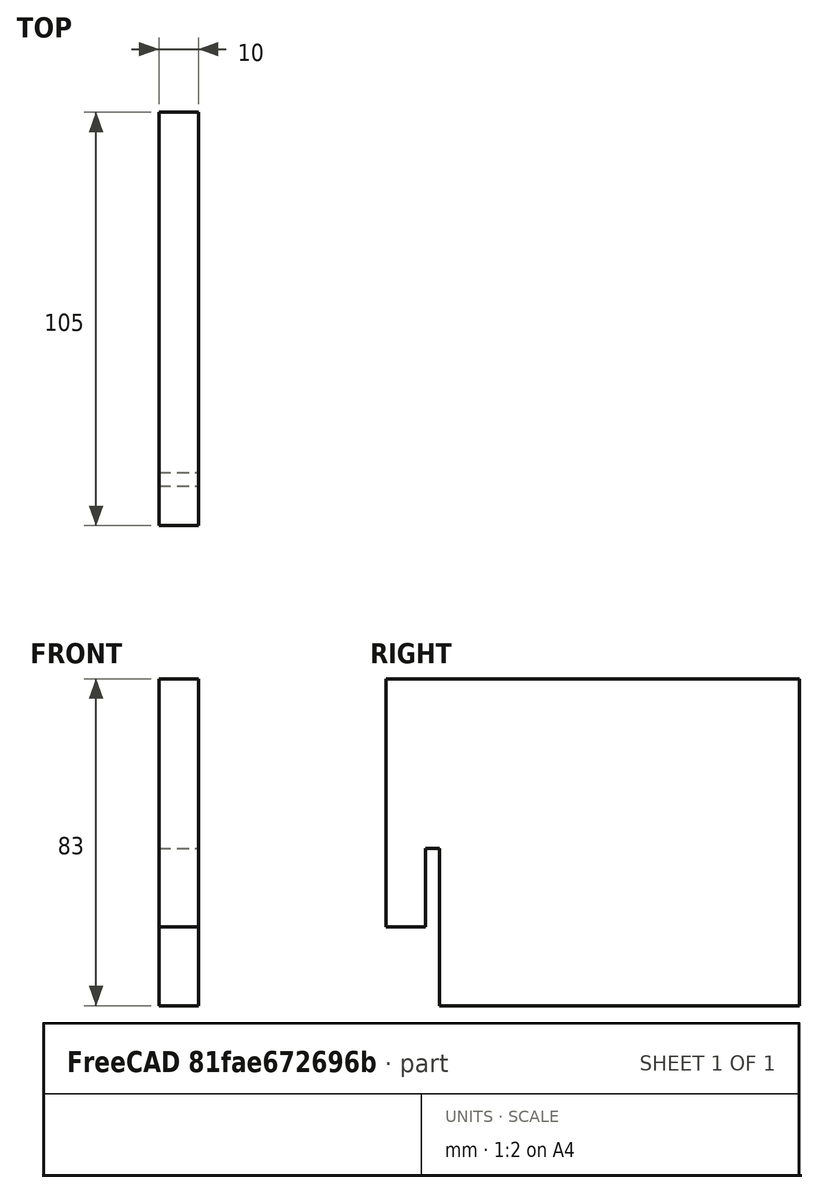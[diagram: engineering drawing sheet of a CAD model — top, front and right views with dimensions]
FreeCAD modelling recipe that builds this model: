
FCSTD DOCUMENT  (FreeCAD 0.15R4669 (Git))
Label: BR_supportMoteurS
License: All rights reserved
LicenseURL: http://en.wikipedia.org/wiki/All_rights_reserved
objects: Sketcher::SketchObject×1, Part::Extrusion×1
note: 2 computed .brp shape members not serialized (recipe doc carries the construction recipe); baked Part::Feature solids carry a one-line shape summary decoded from their .brp

FEATURE [Sketcher::SketchObject] Sketch  label="sketchSupportMoteurS"
  Placement = pos=(0,0,0) rot=(0.57735,0.57735,0.57735;2.0944rad)
  sketch-geometry (8):
    g0: LineSegment StartX=0 StartY=-18 StartZ=0 EndX=-91.5 EndY=-18 EndZ=0
    g1: LineSegment StartX=-105 StartY=65 StartZ=0 EndX=0 EndY=65 EndZ=0
    g2: LineSegment StartX=0 StartY=65 StartZ=0 EndX=0 EndY=-18 EndZ=0
    g3: LineSegment StartX=-91.5 StartY=-18 StartZ=0 EndX=-91.5 EndY=22 EndZ=0
    g4: LineSegment StartX=-91.5 StartY=22 StartZ=0 EndX=-95 EndY=22 EndZ=0
    g5: LineSegment StartX=-95 StartY=22 StartZ=0 EndX=-95 EndY=2 EndZ=0
    g6: LineSegment StartX=-95 StartY=2 StartZ=0 EndX=-105 EndY=2 EndZ=0
    g7: LineSegment StartX=-105 StartY=2 StartZ=0 EndX=-105 EndY=65 EndZ=0
  constraints (24):
    c: Coincident(g1,g2)
    c: Coincident(g2,g0)
    c: Horizontal(g0)
    c: Horizontal(g1)
    c: Vertical(g2)
    c: DistanceX(g0) = -91.5
    c: DistanceY(g-1,g0) = -18
    c: DistanceY(g-1,g1) = 65
    c: PointOnObject(g0,g-2)
    c: Coincident(g3,g0)
    c: Vertical(g3)
    c: Coincident(g4,g3)
    c: Horizontal(g4)
    c: Coincident(g4,g5)
    c: Vertical(g5)
    c: Coincident(g5,g6)
    c: Horizontal(g6)
    c: Coincident(g6,g7)
    c: Vertical(g7)
    c: Coincident(g7,g1)
    c: DistanceX(g4) = -3.5
    c: DistanceY(g3) = 40
    c: DistanceX(g6) = -10
    c: DistanceY(g5) = -20
FEATURE [Part::Extrusion] Extrude  label="supportMoteurS"
  Base = -> Sketch
  Dir = (10,0,0)
  Solid = true
